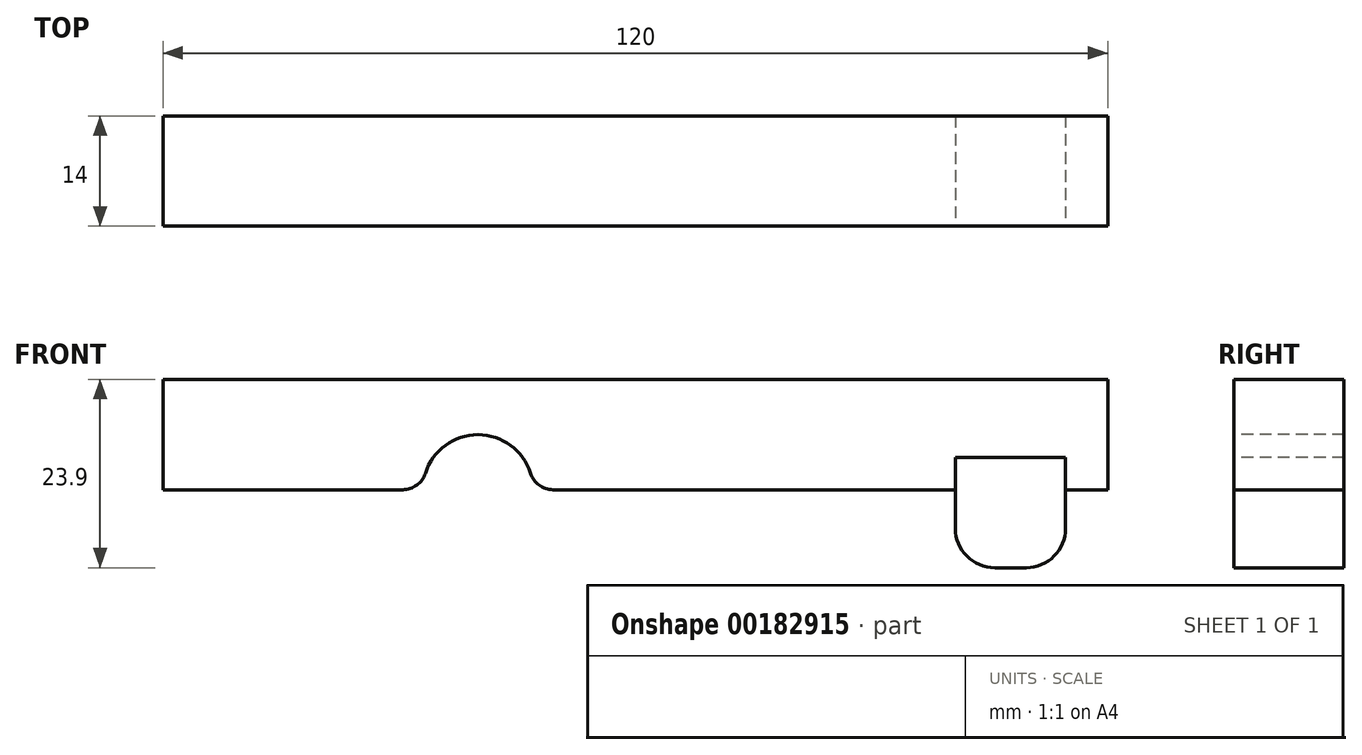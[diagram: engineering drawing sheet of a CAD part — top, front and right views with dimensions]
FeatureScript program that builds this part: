
annotation { "Feature Type Name" : "Feature", "Feature Type Description" : "" }
export const myFeature = defineFeature(function(context is Context, id is Id, definition is map)
    precondition{}
    {
        {
            var Q0;
            Q0=qCreatedBy(makeId("Front.planeOp"),FACE);
            var sketch = newSketch(context, id + "F0", { "sketchPlane" : qUnion([Q0])});
            skLineSegment(sketch, "E0.bottom", {"start": v(60, -7) * mm, "end": v(-60, -7) * mm});
            skLineSegment(sketch, "E0.top", {"start": v(60, 7) * mm, "end": v(-60, 7) * mm});
            skLineSegment(sketch, "E0.left", {"start": v(60, -7) * mm, "end": v(60, 7) * mm});
            skPoint(sketch, "E0.middle", {"position": v(0, 0) * mm});
            skLineSegment(sketch, "E1", {"start": v(-60, 7) * mm, "end": v(-60, -7) * mm});
            skSolve(sketch);
        }
        {
            var Q0;
            Q0=makeQuery(id+"F0.imprint","IMPRINT",FACE,{"disambiguationData":[TD([[makeQuery(id+"F0.imprint","IMPRINT",EDGE,{"derivedFrom":sQuery(id+"F0.wireOp",EDGE,"E0.bottom")}),-1.0]])]});
            extrude(context, id + "F1", {"entities" : qUnion([Q0]), "depth" : 14 * mm});
        }
        {
            var Q0;
            Q0=makeQuery(id+"F1.opExtrude","CAP_FACE",FACE,{"disambiguationData":[OSD([sQuery(id+"F0.wireOp",EDGE,"E0.bottom"),sQuery(id+"F0.wireOp",EDGE,"E0.top"),sQuery(id+"F0.wireOp",EDGE,"E0.left"),sQuery(id+"F0.wireOp",EDGE,"VLBKri8P-oLkN-kY2H-hz3f-YcUiOj6Otxep"),sQuery(id+"F0.wireOp",EDGE,"E1")])],"isStart":false});
            var sketch = newSketch(context, id + "F2", { "sketchPlane" : qUnion([Q0])});
            skCircle(sketch, "E2", {"center": v(-20, -7) * mm, "radius": 7 * mm});
            skSolve(sketch);
        }
        {
            var Q0;
            Q0 = qSketchRegion(id + "F2", true);
            extrude(context, id + "F3", {"entities" : qUnion([Q0]), "operationType" : NewBodyOperationType.REMOVE, "endBound" : BoundingType.THROUGH_ALL, "oppositeDirection" : true, "depth" : 25 * mm});
        }
        {
            var Q0;
            Q0=makeQuery(id+"F3.boolean.opBoolean","INTERSECT",EDGE,{"disambiguationData":[OD(1.0)],"derivedFrom":[makeQuery(id+"F1.opExtrude","SWEPT_FACE",FACE,{"disambiguationData":[OSD([sQuery(id+"F0.wireOp",EDGE,"E0.bottom")])]}),makeQuery(id+"F3.opExtrude","SWEPT_FACE",FACE,{"disambiguationData":[OSD([sQuery(id+"F2.wireOp",EDGE,"E2")])]})]});
            var Q1;
            Q1=makeQuery(id+"F3.boolean.opBoolean","INTERSECT",EDGE,{"disambiguationData":[OD(0.0)],"derivedFrom":[makeQuery(id+"F1.opExtrude","SWEPT_FACE",FACE,{"disambiguationData":[OSD([sQuery(id+"F0.wireOp",EDGE,"E0.bottom")])]}),makeQuery(id+"F3.opExtrude","SWEPT_FACE",FACE,{"disambiguationData":[OSD([sQuery(id+"F2.wireOp",EDGE,"E2")])]})]});
            fillet(context, id + "F4", {"entities" : qUnion([Q0, Q1]), "radius" : 3 * mm, "tangentPropagation" : true, "allowEdgeOverflow" : false});
        }
        {
            var Q0;
            Q0=makeQuery(id+"F1.opExtrude","CAP_FACE",FACE,{"disambiguationData":[OSD([sQuery(id+"F0.wireOp",EDGE,"E0.bottom"),sQuery(id+"F0.wireOp",EDGE,"E0.top"),sQuery(id+"F0.wireOp",EDGE,"E0.left"),sQuery(id+"F0.wireOp",EDGE,"E1")])],"isStart":false});
            var sketch = newSketch(context, id + "F5", { "sketchPlane" : qUnion([Q0])});
            skLineSegment(sketch, "E3.bottom", {"start": v(40.65, -2.9) * mm, "end": v(54.65, -2.9) * mm});
            skLineSegment(sketch, "E3.top", {"start": v(40.65, -16.9) * mm, "end": v(54.65, -16.9) * mm});
            skLineSegment(sketch, "E3.left", {"start": v(40.65, -2.9) * mm, "end": v(40.65, -16.9) * mm});
            skLineSegment(sketch, "E3.right", {"start": v(54.65, -2.9) * mm, "end": v(54.65, -16.9) * mm});
            skSolve(sketch);
        }
        {
            var Q0;
            Q0 = qSketchRegion(id + "F5", true);
            var Q1;
            Q1 = qConstructionFilter(qBodyType(qCreatedBy(id + "F5" ,EDGE), BodyType.WIRE), ConstructionObject.NO);
            extrude(context, id + "F6", {"entities" : qUnion([Q0]), "operationType" : NewBodyOperationType.REMOVE, "surfaceEntities" : qUnion([Q1]), "endBound" : BoundingType.THROUGH_ALL, "oppositeDirection" : true, "depth" : 25 * mm});
        }
        {
            var Q0;
            Q0 = qSketchRegion(id + "F5", true);
            extrude(context, id + "F7", {"entities" : qUnion([Q0]), "oppositeDirection" : true, "depth" : 14 * mm});
        }
        {
            var Q0;
            Q0=makeQuery(id+"F7.opExtrude","SWEPT_EDGE",EDGE,{"disambiguationData":[OSD([sQuery(id+"F5.wireOp",EDGE,"E3.top"),sQuery(id+"F5.wireOp",EDGE,"E3.right")])]});
            var Q1;
            Q1=makeQuery(id+"F7.opExtrude","SWEPT_EDGE",EDGE,{"disambiguationData":[OSD([sQuery(id+"F5.wireOp",EDGE,"E3.top"),sQuery(id+"F5.wireOp",EDGE,"E3.left")])]});
            fillet(context, id + "F8", {"entities" : qUnion([Q0, Q1]), "radius" : 5 * mm, "tangentPropagation" : true, "allowEdgeOverflow" : false});
        }
    });
